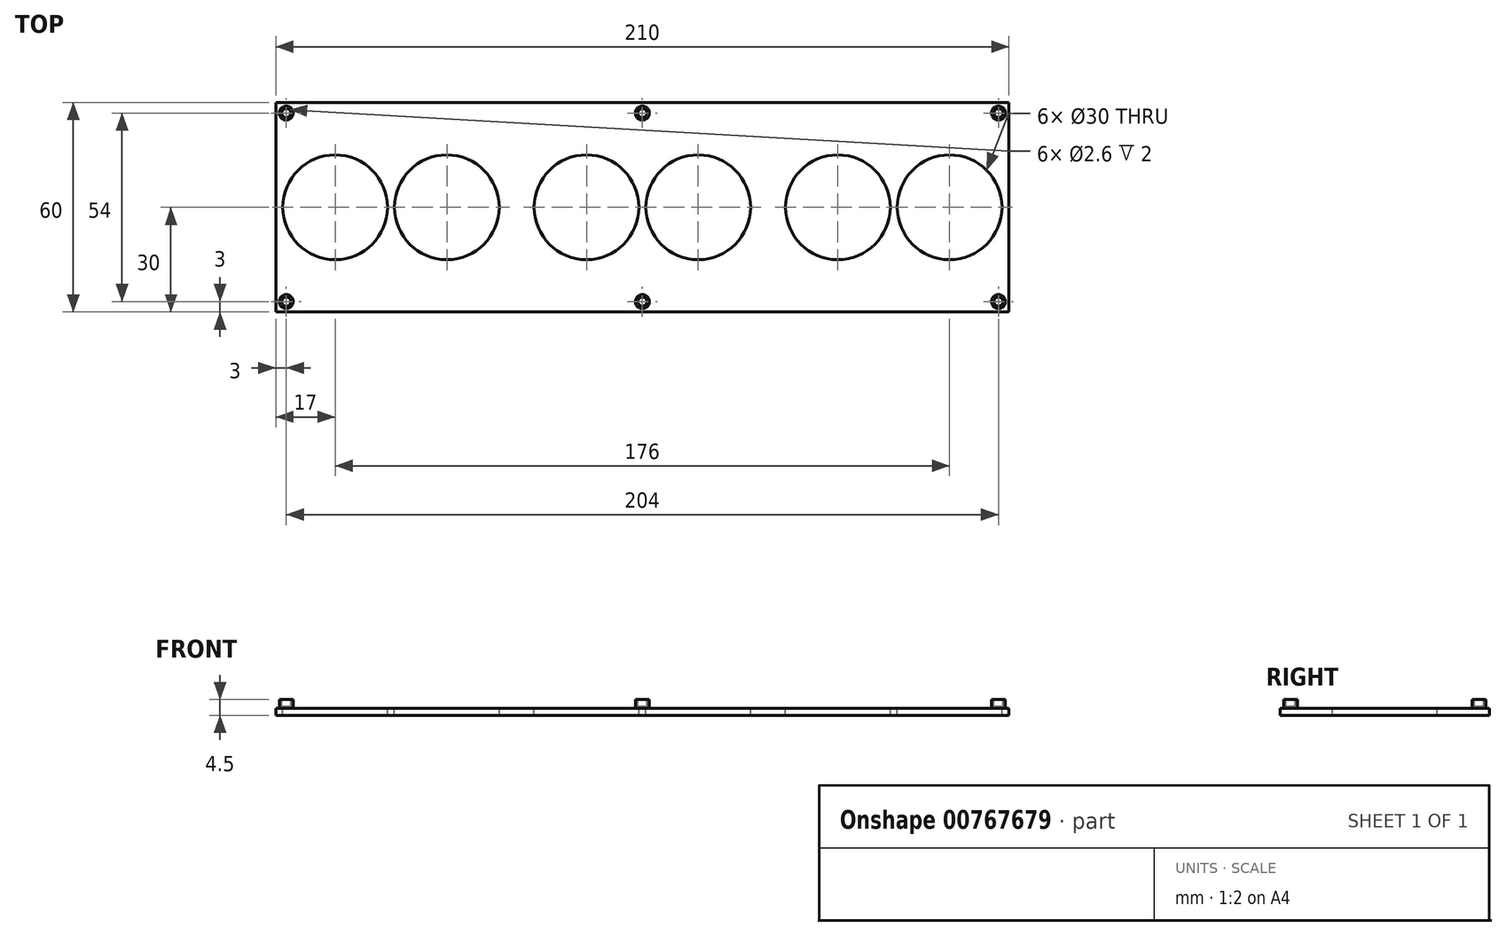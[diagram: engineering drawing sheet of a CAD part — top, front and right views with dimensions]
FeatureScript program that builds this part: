
annotation { "Feature Type Name" : "Feature", "Feature Type Description" : "" }
export const myFeature = defineFeature(function(context is Context, id is Id, definition is map)
    precondition{}
    {
        {
            var Q0;
            Q0=qCreatedBy(makeId("Top.planeOp"),FACE);
            var sketch = newSketch(context, id + "F0", { "sketchPlane" : qUnion([Q0])});
            skLineSegment(sketch, "E0.bottom", {"start": v(-105, 30) * mm, "end": v(105, 30) * mm});
            skLineSegment(sketch, "E0.top", {"start": v(-105, -30) * mm, "end": v(105, -30) * mm});
            skLineSegment(sketch, "E0.left", {"start": v(-105, 30) * mm, "end": v(-105, -30) * mm});
            skLineSegment(sketch, "E0.right", {"start": v(105, 30) * mm, "end": v(105, -30) * mm});
            skPoint(sketch, "E0.middle", {"position": v(0, 0) * mm});
            skSolve(sketch);
        }
        {
            var Q0;
            Q0 = qSketchRegion(id + "F0", true);
            extrude(context, id + "F1", {"entities" : qUnion([Q0]), "depth" : 2 * mm, "offsetDistance" : 25 * mm});
        }
        {
            var Q0;
            Q0=makeQuery(id+"F1.opExtrude","CAP_FACE",FACE,{"disambiguationData":[OSD([sQuery(id+"F0.wireOp",EDGE,"E0.bottom"),sQuery(id+"F0.wireOp",EDGE,"E0.top"),sQuery(id+"F0.wireOp",EDGE,"E0.left"),sQuery(id+"F0.wireOp",EDGE,"E0.right")])],"isStart":false});
            var sketch = newSketch(context, id + "F2", { "sketchPlane" : qUnion([Q0])});
            skCircle(sketch, "E1", {"center": v(-88, 0) * mm, "radius": 15 * mm});
            skPoint(sketch, "E1.centerSnap0", {"position": v(-105, 0) * mm});
            skCircle(sketch, "E2", {"center": v(-56, 0) * mm, "radius": 15 * mm});
            skCircle(sketch, "E3", {"center": v(-16, 0) * mm, "radius": 15 * mm});
            skCircle(sketch, "E4", {"center": v(16, 0) * mm, "radius": 15 * mm});
            skCircle(sketch, "E5", {"center": v(56, 0) * mm, "radius": 15 * mm});
            skCircle(sketch, "E6", {"center": v(88, 0) * mm, "radius": 15 * mm});
            skSolve(sketch);
        }
        {
            var Q0;
            Q0 = qSketchRegion(id + "F2", true);
            extrude(context, id + "F3", {"entities" : qUnion([Q0]), "operationType" : NewBodyOperationType.REMOVE, "oppositeDirection" : true, "depth" : 2 * mm, "offsetDistance" : 25 * mm});
        }
        {
            var Q0;
            Q0=makeQuery(id+"F1.opExtrude","CAP_FACE",FACE,{"disambiguationData":[OSD([sQuery(id+"F0.wireOp",EDGE,"E0.bottom"),sQuery(id+"F0.wireOp",EDGE,"E0.top"),sQuery(id+"F0.wireOp",EDGE,"E0.left"),sQuery(id+"F0.wireOp",EDGE,"E0.right")])],"isStart":false});
            var sketch = newSketch(context, id + "F4", { "sketchPlane" : qUnion([Q0])});
            skCircle(sketch, "E7", {"center": v(-102, -27) * mm, "radius": 2 * mm});
            skCircle(sketch, "E8", {"center": v(-102, 27) * mm, "radius": 2 * mm});
            skCircle(sketch, "E9", {"center": v(102, -27) * mm, "radius": 2 * mm});
            skCircle(sketch, "E10", {"center": v(102, 27) * mm, "radius": 2 * mm});
            skCircle(sketch, "E11", {"center": v(0, 27) * mm, "radius": 2 * mm});
            skCircle(sketch, "E12", {"center": v(0, -27) * mm, "radius": 2 * mm});
            skSolve(sketch);
        }
        {
            var Q0;
            Q0 = qSketchRegion(id + "F4", true);
            extrude(context, id + "F5", {"entities" : qUnion([Q0]), "operationType" : NewBodyOperationType.ADD, "depth" : 2.5 * mm, "offsetDistance" : 25 * mm});
        }
        {
            var Q0;
            Q0=makeQuery(id+"F5.opExtrude","CAP_FACE",FACE,{"disambiguationData":[OSD([sQuery(id+"F4.wireOp",EDGE,"E12")])],"isStart":false});
            var sketch = newSketch(context, id + "F6", { "sketchPlane" : qUnion([Q0])});
            skCircle(sketch, "E13", {"center": v(0, -27) * mm, "radius": 1.3 * mm});
            skSolve(sketch);
        }
        {
            var Q0;
            Q0 = qSketchRegion(id + "F6", true);
            extrude(context, id + "F7", {"entities" : qUnion([Q0]), "operationType" : NewBodyOperationType.REMOVE, "oppositeDirection" : true, "depth" : 2 * mm, "offsetDistance" : 25 * mm});
        }
        {
            var Q0;
            Q0=makeQuery(id+"F5.opExtrude","CAP_FACE",FACE,{"disambiguationData":[OSD([sQuery(id+"F4.wireOp",EDGE,"E7")])],"isStart":false});
            var sketch = newSketch(context, id + "F8", { "sketchPlane" : qUnion([Q0])});
            skCircle(sketch, "E14", {"center": v(-102, -27) * mm, "radius": 1.3 * mm});
            skSolve(sketch);
        }
        {
            var Q0;
            Q0 = qSketchRegion(id + "F8", true);
            extrude(context, id + "F9", {"entities" : qUnion([Q0]), "operationType" : NewBodyOperationType.REMOVE, "oppositeDirection" : true, "depth" : 2 * mm, "offsetDistance" : 25 * mm});
        }
        {
            var Q0;
            Q0=makeQuery(id+"F5.opExtrude","CAP_FACE",FACE,{"disambiguationData":[OSD([sQuery(id+"F4.wireOp",EDGE,"E8")])],"isStart":false});
            var sketch = newSketch(context, id + "F10", { "sketchPlane" : qUnion([Q0])});
            skCircle(sketch, "E15", {"center": v(-102, 27) * mm, "radius": 1.3 * mm});
            skSolve(sketch);
        }
        {
            var Q0;
            Q0 = qSketchRegion(id + "F10", true);
            extrude(context, id + "F11", {"entities" : qUnion([Q0]), "operationType" : NewBodyOperationType.REMOVE, "oppositeDirection" : true, "depth" : 2 * mm, "offsetDistance" : 25 * mm});
        }
        {
            var Q0;
            Q0=makeQuery(id+"F5.opExtrude","CAP_FACE",FACE,{"disambiguationData":[OSD([sQuery(id+"F4.wireOp",EDGE,"E11")])],"isStart":false});
            var sketch = newSketch(context, id + "F12", { "sketchPlane" : qUnion([Q0])});
            skCircle(sketch, "E16", {"center": v(0, 27) * mm, "radius": 1.3 * mm});
            skSolve(sketch);
        }
        {
            var Q0;
            Q0 = qSketchRegion(id + "F12", true);
            extrude(context, id + "F13", {"entities" : qUnion([Q0]), "operationType" : NewBodyOperationType.REMOVE, "oppositeDirection" : true, "depth" : 2 * mm, "offsetDistance" : 25 * mm});
        }
        {
            var Q0;
            Q0=makeQuery(id+"F5.opExtrude","CAP_FACE",FACE,{"disambiguationData":[OSD([sQuery(id+"F4.wireOp",EDGE,"E10")])],"isStart":false});
            var sketch = newSketch(context, id + "F14", { "sketchPlane" : qUnion([Q0])});
            skCircle(sketch, "E17", {"center": v(102, 27) * mm, "radius": 1.3 * mm});
            skSolve(sketch);
        }
        {
            var Q0;
            Q0 = qSketchRegion(id + "F14", true);
            extrude(context, id + "F15", {"entities" : qUnion([Q0]), "operationType" : NewBodyOperationType.REMOVE, "oppositeDirection" : true, "depth" : 2 * mm, "offsetDistance" : 25 * mm});
        }
        {
            var Q0;
            Q0=makeQuery(id+"F5.opExtrude","CAP_FACE",FACE,{"disambiguationData":[OSD([sQuery(id+"F4.wireOp",EDGE,"E9")])],"isStart":false});
            var sketch = newSketch(context, id + "F16", { "sketchPlane" : qUnion([Q0])});
            skCircle(sketch, "E18", {"center": v(102, -27) * mm, "radius": 1.3 * mm});
            skSolve(sketch);
        }
        {
            var Q0;
            Q0 = qSketchRegion(id + "F16", true);
            extrude(context, id + "F17", {"entities" : qUnion([Q0]), "operationType" : NewBodyOperationType.REMOVE, "oppositeDirection" : true, "depth" : 2 * mm, "offsetDistance" : 25 * mm});
        }
    });
